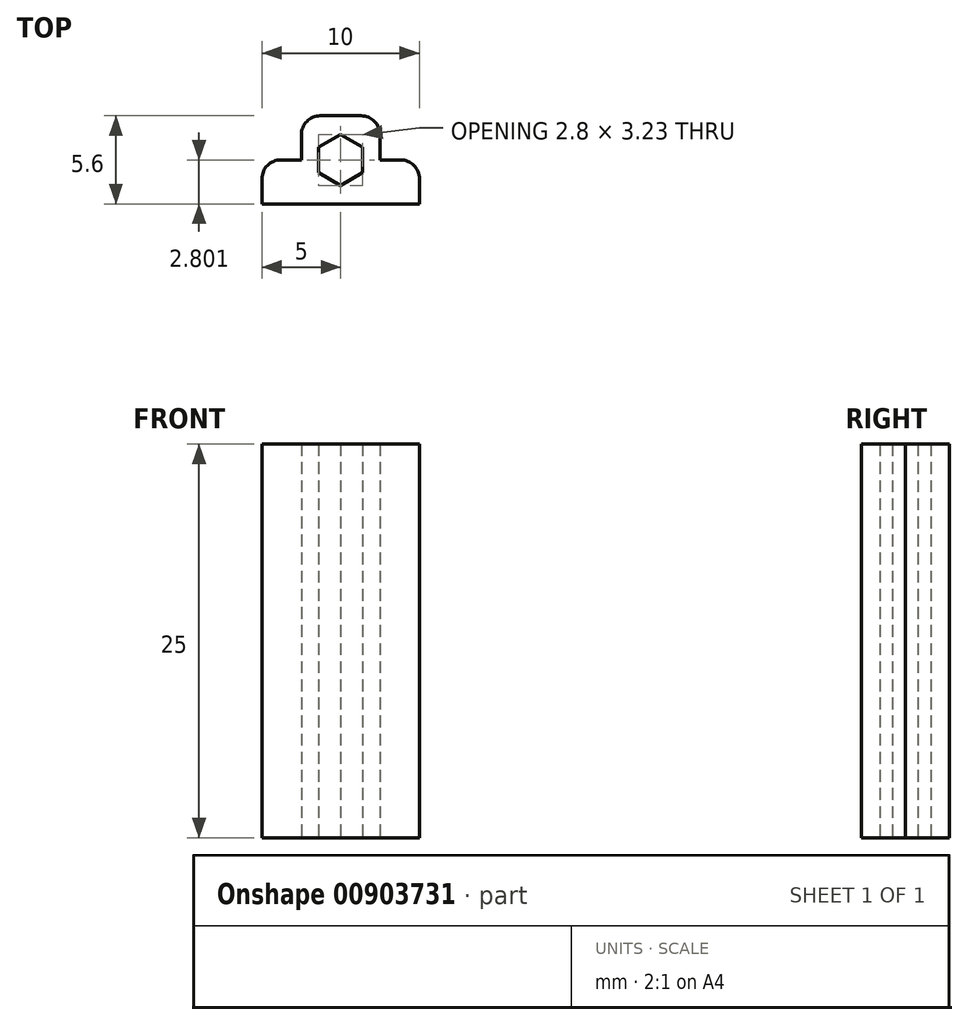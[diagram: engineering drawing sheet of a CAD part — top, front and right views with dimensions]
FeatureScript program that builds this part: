
annotation { "Feature Type Name" : "Feature", "Feature Type Description" : "" }
export const myFeature = defineFeature(function(context is Context, id is Id, definition is map)
    precondition{}
    {
        {
            var Q0;
            Q0=qCreatedBy(makeId("Top.planeOp"),FACE);
            var sketch = newSketch(context, id + "F0", { "sketchPlane" : qUnion([Q0])});
            skLineSegment(sketch, "E0", {"start": v(0, 0) * mm, "end": v(5, 0) * mm});
            skLineSegment(sketch, "E1", {"start": v(5, 0) * mm, "end": v(5, 2.8) * mm});
            skLineSegment(sketch, "E2", {"start": v(5, 2.8) * mm, "end": v(2.5, 2.8) * mm});
            skLineSegment(sketch, "E3", {"start": v(-5, 2.8) * mm, "end": v(-5, 0) * mm});
            skLineSegment(sketch, "E4", {"start": v(-5, 0) * mm, "end": v(0, 0) * mm});
            skLineSegment(sketch, "E5", {"start": v(2.5, 2.8) * mm, "end": v(2.5, 5.6) * mm});
            skLineSegment(sketch, "E6", {"start": v(2.5, 5.6) * mm, "end": v(-2.5, 5.6) * mm});
            skLineSegment(sketch, "E7", {"start": v(-2.5, 5.6) * mm, "end": v(-2.5, 2.8) * mm});
            skLineSegment(sketch, "E8.trimOffspring", {"start": v(-2.5, 2.8) * mm, "end": v(-5, 2.8) * mm});
            skCircle(sketch, "E9.cCircle", {"center": v(0, 2.8) * mm, "radius": 1.4 * mm, "construction": true});
            skLineSegment(sketch, "E9.0", {"start": v(1.4, 3.6) * mm, "end": v(1.4, 2) * mm});
            skLineSegment(sketch, "E9.1", {"start": v(1.4, 2) * mm, "end": v(0, 1.18) * mm});
            skLineSegment(sketch, "E9.2", {"start": v(0, 1.18) * mm, "end": v(-1.4, 2) * mm});
            skLineSegment(sketch, "E9.3", {"start": v(-1.4, 2) * mm, "end": v(-1.4, 3.6) * mm});
            skLineSegment(sketch, "E9.4", {"start": v(-1.4, 3.6) * mm, "end": v(0, 4.42) * mm});
            skLineSegment(sketch, "E9.5", {"start": v(0, 4.42) * mm, "end": v(1.4, 3.6) * mm});
            skPoint(sketch, "E9.0.midPoint", {"position": v(1.4, 2.8) * mm});
            skSolve(sketch);
        }
        {
            var Q0;
            Q0=makeQuery(id+"F0.imprint","IMPRINT",FACE,{"disambiguationData":[TD([[makeQuery(id+"F0.imprint","IMPRINT",EDGE,{"derivedFrom":sQuery(id+"F0.wireOp",EDGE,"E0")}),1.0]])]});
            extrude(context, id + "F1", {"entities" : qUnion([Q0]), "depth" : 25 * mm, "offsetDistance" : 25 * mm});
        }
        {
            var Q0;
            Q0=makeQuery(id+"F1.opExtrude","SWEPT_EDGE",EDGE,{"disambiguationData":[OSD([sQuery(id+"F0.wireOp",EDGE,"E6"),sQuery(id+"F0.wireOp",EDGE,"E7")])]});
            var Q1;
            Q1=makeQuery(id+"F1.opExtrude","SWEPT_EDGE",EDGE,{"disambiguationData":[OSD([sQuery(id+"F0.wireOp",EDGE,"E5"),sQuery(id+"F0.wireOp",EDGE,"E6")])]});
            var Q2;
            Q2=makeQuery(id+"F1.opExtrude","SWEPT_EDGE",EDGE,{"disambiguationData":[OSD([sQuery(id+"F0.wireOp",EDGE,"E1"),sQuery(id+"F0.wireOp",EDGE,"E2")])]});
            var Q3;
            Q3=makeQuery(id+"F1.opExtrude","SWEPT_EDGE",EDGE,{"disambiguationData":[OSD([sQuery(id+"F0.wireOp",EDGE,"E3"),sQuery(id+"F0.wireOp",EDGE,"E8.trimOffspring")])]});
            fillet(context, id + "F2", {"entities" : qUnion([Q0, Q1, Q2, Q3]), "radius" : 1.2 * mm, "tangentPropagation" : true, "allowEdgeOverflow" : false});
        }
    });
